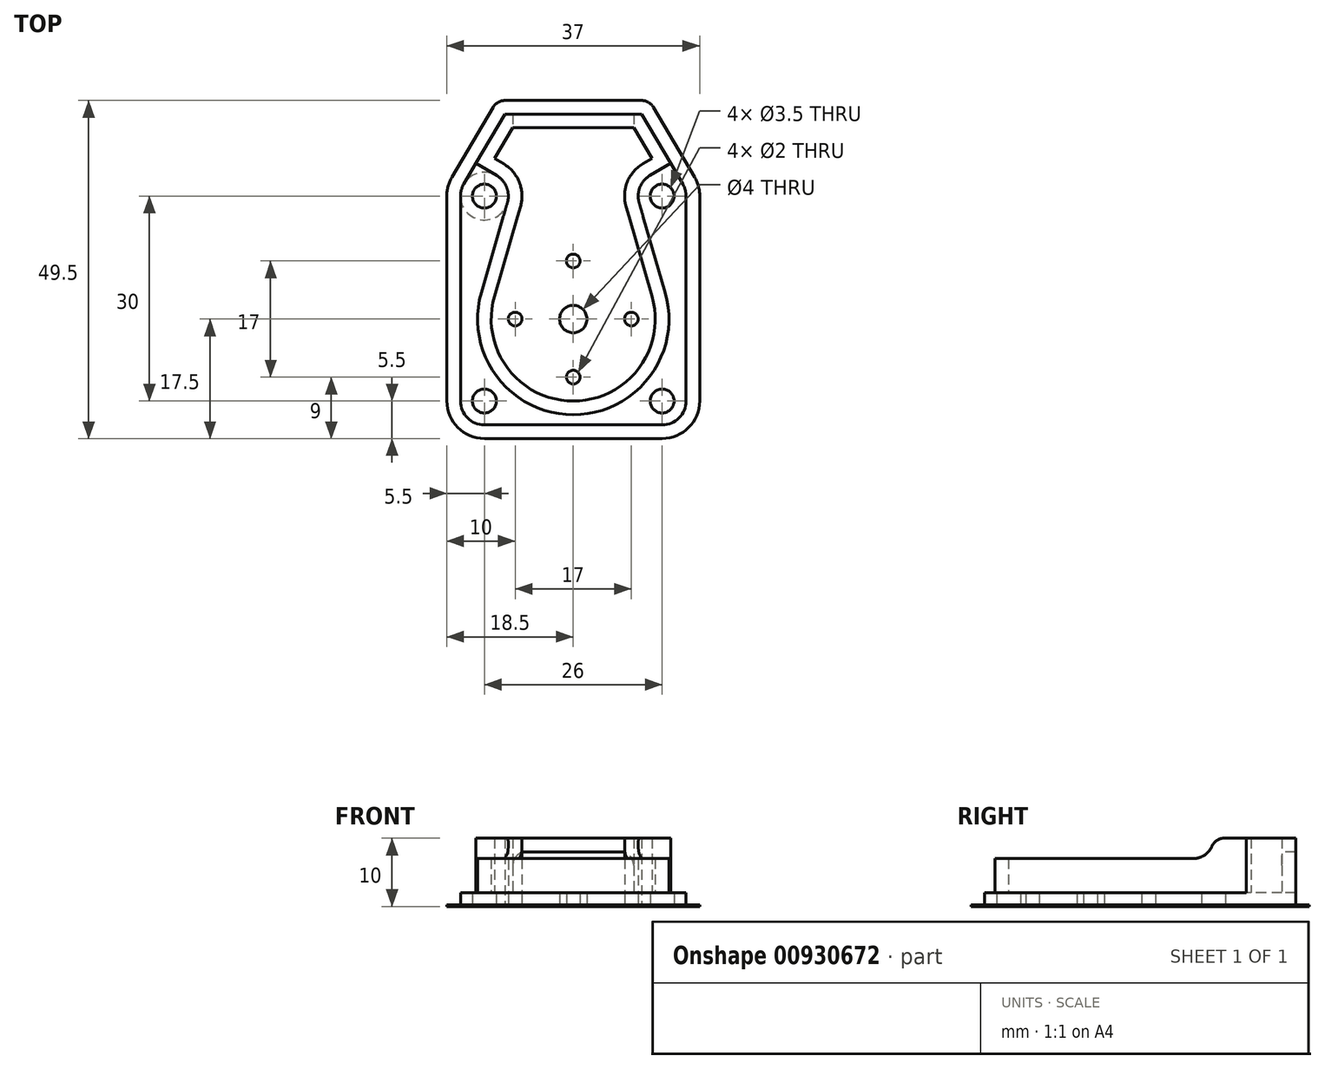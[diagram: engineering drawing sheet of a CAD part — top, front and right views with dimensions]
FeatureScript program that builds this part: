
annotation { "Feature Type Name" : "Feature", "Feature Type Description" : "" }
export const myFeature = defineFeature(function(context is Context, id is Id, definition is map)
    precondition{}
    {
        {
            var Q0;
            Q0=qCreatedBy(makeId("Top.planeOp"),FACE);
            var sketch = newSketch(context, id + "F0", { "sketchPlane" : qUnion([Q0])});
            skCircle(sketch, "E0", {"center": v(0, 0) * mm, "radius": 1.75 * mm});
            skCircle(sketch, "E1", {"center": v(0, 30) * mm, "radius": 1.75 * mm});
            skCircle(sketch, "E2", {"center": v(26, 30) * mm, "radius": 1.75 * mm});
            skCircle(sketch, "E3", {"center": v(26, 0) * mm, "radius": 1.75 * mm});
            skLineSegment(sketch, "E4.left", {"start": v(0, 30) * mm, "end": v(0, 0) * mm, "construction": true});
            skCircle(sketch, "E5", {"center": v(13, 12) * mm, "radius": 9.85 * mm, "construction": true});
            skLineSegment(sketch, "E6", {"start": v(13, 21.85) * mm, "end": v(13, 2.15) * mm, "construction": true});
            skLineSegment(sketch, "E7", {"start": v(3.15, 12) * mm, "end": v(22.85, 12) * mm, "construction": true});
            skCircle(sketch, "E8", {"center": v(13, 12) * mm, "radius": 2 * mm});
            skCircle(sketch, "E9", {"center": v(4.5, 12) * mm, "radius": 1 * mm});
            skCircle(sketch, "E10", {"center": v(21.5, 12) * mm, "radius": 1 * mm});
            skCircle(sketch, "E11", {"center": v(13, 20.5) * mm, "radius": 1 * mm});
            skCircle(sketch, "E12", {"center": v(13, 3.5) * mm, "radius": 1 * mm});
            skLineSegment(sketch, "E13", {"start": v(3, 42) * mm, "end": v(23, 42) * mm});
            skLineSegment(sketch, "E14", {"start": v(0, 30) * mm, "end": v(26, 30) * mm, "construction": true});
            skLineSegment(sketch, "E15", {"start": v(0, 0) * mm, "end": v(26, 0) * mm, "construction": true});
            skLineSegment(sketch, "E16.trimOffspring", {"start": v(-3.02, 31.77) * mm, "end": v(3, 42) * mm});
            skLineSegment(sketch, "E17.trimOffspring", {"start": v(29.02, 31.77) * mm, "end": v(23, 42) * mm});
            skLineSegment(sketch, "E18", {"start": v(26, 30) * mm, "end": v(26, 0) * mm, "construction": true});
            skLineSegment(sketch, "E19", {"start": v(-3.5, 30) * mm, "end": v(-3.5, 0) * mm});
            skLineSegment(sketch, "E20", {"start": v(0, -3.5) * mm, "end": v(26, -3.5) * mm});
            skLineSegment(sketch, "E21", {"start": v(29.5, 30) * mm, "end": v(29.5, 0) * mm});
            skArc(sketch, "E22", {"start": v(-3.5, 0) * mm, "mid": v(-2.47, -2.47) * mm, "end": v(0, -3.5) * mm});
            skArc(sketch, "E23", {"start": v(26, -3.5) * mm, "mid": v(28.47, -2.47) * mm, "end": v(29.5, 0) * mm});
            skArc(sketch, "E24", {"start": v(-3.02, 31.77) * mm, "mid": v(-3.38, 30.92) * mm, "end": v(-3.5, 30) * mm});
            skArc(sketch, "E25", {"start": v(29.5, 30) * mm, "mid": v(29.38, 30.92) * mm, "end": v(29.02, 31.77) * mm});
            skSolve(sketch);
        }
        {
            var Q0;
            Q0=qSketchRegion(id+"F0",true);
            extrude(context, id + "F1", {"entities" : qUnion([Q0]), "depth" : 2 * mm, "offsetDistance" : 25 * mm});
        }
        {
            var Q0;
            Q0=makeQuery(id+"F1.opExtrude","CAP_FACE",FACE,{"disambiguationData":[OSD([sQuery(id+"F0.wireOp",EDGE,"E0"),sQuery(id+"F0.wireOp",EDGE,"E1"),sQuery(id+"F0.wireOp",EDGE,"E2"),sQuery(id+"F0.wireOp",EDGE,"E3"),sQuery(id+"F0.wireOp",EDGE,"E8"),sQuery(id+"F0.wireOp",EDGE,"E9"),sQuery(id+"F0.wireOp",EDGE,"E10"),sQuery(id+"F0.wireOp",EDGE,"E11"),sQuery(id+"F0.wireOp",EDGE,"E12"),sQuery(id+"F0.wireOp",EDGE,"E13"),sQuery(id+"F0.wireOp",EDGE,"E16.trimOffspring"),sQuery(id+"F0.wireOp",EDGE,"E17.trimOffspring"),sQuery(id+"F0.wireOp",EDGE,"E19"),sQuery(id+"F0.wireOp",EDGE,"E20"),sQuery(id+"F0.wireOp",EDGE,"E21"),sQuery(id+"F0.wireOp",EDGE,"E22"),sQuery(id+"F0.wireOp",EDGE,"E23"),sQuery(id+"F0.wireOp",EDGE,"E24"),sQuery(id+"F0.wireOp",EDGE,"E25")])],"isStart":false});
            var sketch = newSketch(context, id + "F2", { "sketchPlane" : qUnion([Q0])});
            skLineSegment(sketch, "E26", {"start": v(0, 30) * mm, "end": v(26, 30) * mm, "construction": true});
            skLineSegment(sketch, "E27", {"start": v(3, 42) * mm, "end": v(23, 42) * mm});
            skLineSegment(sketch, "E28", {"start": v(23, 42) * mm, "end": v(27.24, 34.8) * mm});
            skLineSegment(sketch, "E29", {"start": v(27.24, 34.8) * mm, "end": v(24.23, 33.02) * mm});
            skArc(sketch, "E30", {"start": v(24.23, 33.02) * mm, "mid": v(22.75, 31.3) * mm, "end": v(22.64, 29.02) * mm});
            skArc(sketch, "E31", {"start": v(3.36, 29.02) * mm, "mid": v(3.25, 31.3) * mm, "end": v(1.77, 33.02) * mm});
            skLineSegment(sketch, "E32", {"start": v(3, 42) * mm, "end": v(-1.24, 34.8) * mm});
            skLineSegment(sketch, "E33", {"start": v(-1.24, 34.8) * mm, "end": v(1.77, 33.02) * mm});
            skLineSegment(sketch, "E34", {"start": v(4.14, 40) * mm, "end": v(1.5, 35.5) * mm});
            skLineSegment(sketch, "E35", {"start": v(1.5, 35.5) * mm, "end": v(2.79, 34.74) * mm});
            skLineSegment(sketch, "E36", {"start": v(4.14, 40) * mm, "end": v(21.86, 40) * mm});
            skLineSegment(sketch, "E37", {"start": v(21.86, 40) * mm, "end": v(24.5, 35.5) * mm});
            skLineSegment(sketch, "E38", {"start": v(24.5, 35.5) * mm, "end": v(23.21, 34.74) * mm});
            skArc(sketch, "E39", {"start": v(5.28, 28.47) * mm, "mid": v(5.11, 32.03) * mm, "end": v(2.79, 34.74) * mm});
            skArc(sketch, "E40", {"start": v(23.21, 34.74) * mm, "mid": v(20.89, 32.03) * mm, "end": v(20.72, 28.47) * mm});
            skArc(sketch, "E41", {"start": v(1.48, 15.34) * mm, "mid": v(13, 0) * mm, "end": v(24.52, 15.34) * mm});
            skArc(sketch, "E42", {"start": v(-0.45, 15.9) * mm, "mid": v(13, -2) * mm, "end": v(26.45, 15.9) * mm});
            skLineSegment(sketch, "E43", {"start": v(-0.45, 15.9) * mm, "end": v(3.36, 29.02) * mm});
            skLineSegment(sketch, "E44", {"start": v(22.64, 29.02) * mm, "end": v(26.45, 15.9) * mm});
            skLineSegment(sketch, "E45", {"start": v(20.72, 28.47) * mm, "end": v(24.52, 15.34) * mm});
            skLineSegment(sketch, "E46", {"start": v(5.28, 28.47) * mm, "end": v(1.48, 15.34) * mm});
            skSolve(sketch);
        }
        {
            var Q0;
            Q0=qSketchRegion(id+"F2",true);
            extrude(context, id + "F3", {"entities" : qUnion([Q0]), "operationType" : NewBodyOperationType.ADD, "depth" : 8 * mm, "offsetDistance" : 25 * mm});
        }
        {
            var Q0;
            Q0=makeQuery(id+"F3.opExtrude","SWEPT_FACE",FACE,{"disambiguationData":[OSD([sQuery(id+"F2.wireOp",EDGE,"E36")])]});
            var sketch = newSketch(context, id + "F4", { "sketchPlane" : qUnion([Q0])});
            skLineSegment(sketch, "E47.bottom", {"start": v(4.14, 2) * mm, "end": v(21.86, 2) * mm});
            skLineSegment(sketch, "E47.top", {"start": v(4.14, 8) * mm, "end": v(21.86, 8) * mm});
            skLineSegment(sketch, "E47.left", {"start": v(4.14, 2) * mm, "end": v(4.14, 8) * mm});
            skLineSegment(sketch, "E47.right", {"start": v(21.86, 2) * mm, "end": v(21.86, 8) * mm});
            skSolve(sketch);
        }
        {
            var Q0;
            Q0=qSketchRegion(id+"F4",true);
            extrude(context, id + "F5", {"entities" : qUnion([Q0]), "operationType" : NewBodyOperationType.REMOVE, "endBound" : BoundingType.UP_TO_NEXT, "oppositeDirection" : true, "depth" : 25 * mm, "offsetDistance" : 25 * mm});
        }
        {
            var Q0;
            Q0=makeQuery(id+"F5.boolean.opBoolean","COPY",EDGE,{"derivedFrom":makeQuery(id+"F5.opExtrude","SWEPT_EDGE",EDGE,{"disambiguationData":[OSD([sQuery(id+"F2.wireOp",EDGE,"E34"),sQuery(id+"F2.wireOp",EDGE,"E36"),sQuery(id+"F4.wireOp",EDGE,"E47.top"),sQuery(id+"F4.wireOp",EDGE,"E47.left")])]})});
            var Q1;
            Q1=makeQuery(id+"FvPu7uBZYHSXlxQ_1.boolean.opBoolean","COPY",EDGE,{"derivedFrom":makeQuery(id+"FvPu7uBZYHSXlxQ_1.opExtrude","SWEPT_EDGE",EDGE,{"disambiguationData":[OSD([sQuery(id+"F2.wireOp",EDGE,"87owH7vI-DY4W-UaA8-oZaw-rFrzevB4dvaM"),sQuery(id+"F2.wireOp",EDGE,"E39"),sQuery(id+"FQrBlxE3tJIOwN5_1.wireOp",EDGE,"wGyyUJUZ-AgT6-l7fz-nEv1-yPwmvjUjWFtQ.top"),sQuery(id+"FQrBlxE3tJIOwN5_1.wireOp",EDGE,"wGyyUJUZ-AgT6-l7fz-nEv1-yPwmvjUjWFtQ.right")])]})});
            var Q2;
            Q2=makeQuery(id+"FvPu7uBZYHSXlxQ_1.boolean.opBoolean","COPY",EDGE,{"derivedFrom":makeQuery(id+"FvPu7uBZYHSXlxQ_1.opExtrude","SWEPT_EDGE",EDGE,{"disambiguationData":[OSD([sQuery(id+"F2.wireOp",EDGE,"87owH7vI-DY4W-UaA8-oZaw-rFrzevB4dvaM"),sQuery(id+"F2.wireOp",EDGE,"E40"),sQuery(id+"FQrBlxE3tJIOwN5_1.wireOp",EDGE,"wGyyUJUZ-AgT6-l7fz-nEv1-yPwmvjUjWFtQ.top"),sQuery(id+"FQrBlxE3tJIOwN5_1.wireOp",EDGE,"wGyyUJUZ-AgT6-l7fz-nEv1-yPwmvjUjWFtQ.left")])]})});
            var Q3;
            Q3=makeQuery(id+"F5.boolean.opBoolean","COPY",EDGE,{"derivedFrom":makeQuery(id+"F5.opExtrude","SWEPT_EDGE",EDGE,{"disambiguationData":[OSD([sQuery(id+"F2.wireOp",EDGE,"E36"),sQuery(id+"F2.wireOp",EDGE,"E37"),sQuery(id+"F4.wireOp",EDGE,"E47.top"),sQuery(id+"F4.wireOp",EDGE,"E47.right")])]})});
            fillet(context, id + "F6", {"entities" : qUnion([Q0, Q1, Q2, Q3]), "radius" : 2 * mm, "tangentPropagation" : true, "allowEdgeOverflow" : false});
        }
        {
            var Q0;
            Q0=makeQuery(id+"F3.opExtrude","CAP_FACE",FACE,{"disambiguationData":[OSD([sQuery(id+"F2.wireOp",EDGE,"87owH7vI-DY4W-UaA8-oZaw-rFrzevB4dvaM"),sQuery(id+"F2.wireOp",EDGE,"E27"),sQuery(id+"F2.wireOp",EDGE,"E28"),sQuery(id+"F2.wireOp",EDGE,"E29"),sQuery(id+"F2.wireOp",EDGE,"E30"),sQuery(id+"F2.wireOp",EDGE,"E31"),sQuery(id+"F2.wireOp",EDGE,"E32"),sQuery(id+"F2.wireOp",EDGE,"E33"),sQuery(id+"F2.wireOp",EDGE,"E34"),sQuery(id+"F2.wireOp",EDGE,"E35"),sQuery(id+"F2.wireOp",EDGE,"E36"),sQuery(id+"F2.wireOp",EDGE,"E37"),sQuery(id+"F2.wireOp",EDGE,"E38"),sQuery(id+"F2.wireOp",EDGE,"E39"),sQuery(id+"F2.wireOp",EDGE,"E40"),sQuery(id+"F2.wireOp",EDGE,"E41"),sQuery(id+"F2.wireOp",EDGE,"E42"),sQuery(id+"F2.wireOp",EDGE,"E43"),sQuery(id+"F2.wireOp",EDGE,"E44"),sQuery(id+"F2.wireOp",EDGE,"n5o2zeqW-Y6Ct-pq06-zOnF-6KBVIWVYcsxy"),sQuery(id+"F2.wireOp",EDGE,"E45"),sQuery(id+"F2.wireOp",EDGE,"E46")])],"isStart":false});
            var sketch = newSketch(context, id + "F7", { "sketchPlane" : qUnion([Q0])});
            skLineSegment(sketch, "E48", {"start": v(5.28, 28.47) * mm, "end": v(1.48, 15.34) * mm});
            skLineSegment(sketch, "E49", {"start": v(3.36, 29.02) * mm, "end": v(-0.45, 15.9) * mm});
            skLineSegment(sketch, "E50", {"start": v(20.72, 28.47) * mm, "end": v(24.52, 15.34) * mm});
            skLineSegment(sketch, "E51", {"start": v(22.64, 29.02) * mm, "end": v(26.45, 15.9) * mm});
            skArc(sketch, "E52", {"start": v(1.48, 15.34) * mm, "mid": v(13, 0) * mm, "end": v(24.52, 15.34) * mm});
            skArc(sketch, "E53", {"start": v(-0.45, 15.9) * mm, "mid": v(13, -2) * mm, "end": v(26.45, 15.9) * mm});
            skLineSegment(sketch, "E54", {"start": v(3.5, 30) * mm, "end": v(5.5, 30) * mm});
            skLineSegment(sketch, "E55", {"start": v(20.5, 30) * mm, "end": v(22.5, 30) * mm});
            skArc(sketch, "E56", {"start": v(5.28, 28.47) * mm, "mid": v(5.45, 29.23) * mm, "end": v(5.5, 30) * mm});
            skArc(sketch, "E57", {"start": v(3.36, 29.02) * mm, "mid": v(3.47, 29.5) * mm, "end": v(3.5, 30) * mm});
            skArc(sketch, "E58", {"start": v(20.5, 30) * mm, "mid": v(20.55, 29.23) * mm, "end": v(20.72, 28.47) * mm});
            skArc(sketch, "E59", {"start": v(22.5, 30) * mm, "mid": v(22.53, 29.5) * mm, "end": v(22.64, 29.02) * mm});
            skSolve(sketch);
        }
        {
            var Q0;
            Q0=qSketchRegion(id+"F7",true);
            extrude(context, id + "F8", {"entities" : qUnion([Q0]), "operationType" : NewBodyOperationType.REMOVE, "oppositeDirection" : true, "depth" : 3 * mm, "offsetDistance" : 25 * mm});
        }
        {
            var Q0;
            Q0=makeQuery(id+"F8.boolean.opBoolean","COPY",EDGE,{"derivedFrom":makeQuery(id+"F8.opExtrude","CAP_EDGE",EDGE,{"disambiguationData":[OSD([sQuery(id+"F7.wireOp",EDGE,"E54")])],"isStart":false})});
            var Q1;
            Q1=makeQuery(id+"F8.boolean.opBoolean","COPY",EDGE,{"derivedFrom":makeQuery(id+"F8.opExtrude","CAP_EDGE",EDGE,{"disambiguationData":[OSD([sQuery(id+"F7.wireOp",EDGE,"E55")])],"isStart":false})});
            fillet(context, id + "F9", {"entities" : qUnion([Q0, Q1]), "radius" : 3 * mm, "tangentPropagation" : true, "allowEdgeOverflow" : false});
        }
        {
            var Q0;
            Q0=makeQuery(id+"F9.opFillet","BLEND_EDGE",EDGE,{"blendedFrom":[makeQuery(id+"F8.boolean.opBoolean","COPY",EDGE,{"derivedFrom":makeQuery(id+"F8.opExtrude","CAP_EDGE",EDGE,{"disambiguationData":[OSD([sQuery(id+"F7.wireOp",EDGE,"E54")])],"isStart":false})}),makeQuery(id+"F3.opExtrude","CAP_FACE",FACE,{"disambiguationData":[OSD([sQuery(id+"F2.wireOp",EDGE,"E27"),sQuery(id+"F2.wireOp",EDGE,"E28"),sQuery(id+"F2.wireOp",EDGE,"E29"),sQuery(id+"F2.wireOp",EDGE,"E30"),sQuery(id+"F2.wireOp",EDGE,"E31"),sQuery(id+"F2.wireOp",EDGE,"E32"),sQuery(id+"F2.wireOp",EDGE,"E33"),sQuery(id+"F2.wireOp",EDGE,"E34"),sQuery(id+"F2.wireOp",EDGE,"E35"),sQuery(id+"F2.wireOp",EDGE,"E36"),sQuery(id+"F2.wireOp",EDGE,"E37"),sQuery(id+"F2.wireOp",EDGE,"E38"),sQuery(id+"F2.wireOp",EDGE,"E39"),sQuery(id+"F2.wireOp",EDGE,"E40"),sQuery(id+"F2.wireOp",EDGE,"E41"),sQuery(id+"F2.wireOp",EDGE,"E42"),sQuery(id+"F2.wireOp",EDGE,"E43"),sQuery(id+"F2.wireOp",EDGE,"E44"),sQuery(id+"F2.wireOp",EDGE,"E45"),sQuery(id+"F2.wireOp",EDGE,"E46")])],"isStart":false})],"blendedInto":[makeQuery(id+"F3.opExtrude","CAP_FACE",FACE,{"disambiguationData":[OSD([sQuery(id+"F2.wireOp",EDGE,"E27"),sQuery(id+"F2.wireOp",EDGE,"E28"),sQuery(id+"F2.wireOp",EDGE,"E29"),sQuery(id+"F2.wireOp",EDGE,"E30"),sQuery(id+"F2.wireOp",EDGE,"E31"),sQuery(id+"F2.wireOp",EDGE,"E32"),sQuery(id+"F2.wireOp",EDGE,"E33"),sQuery(id+"F2.wireOp",EDGE,"E34"),sQuery(id+"F2.wireOp",EDGE,"E35"),sQuery(id+"F2.wireOp",EDGE,"E36"),sQuery(id+"F2.wireOp",EDGE,"E37"),sQuery(id+"F2.wireOp",EDGE,"E38"),sQuery(id+"F2.wireOp",EDGE,"E39"),sQuery(id+"F2.wireOp",EDGE,"E40"),sQuery(id+"F2.wireOp",EDGE,"E41"),sQuery(id+"F2.wireOp",EDGE,"E42"),sQuery(id+"F2.wireOp",EDGE,"E43"),sQuery(id+"F2.wireOp",EDGE,"E44"),sQuery(id+"F2.wireOp",EDGE,"E45"),sQuery(id+"F2.wireOp",EDGE,"E46")])],"isStart":false})]});
            var Q1;
            Q1=makeQuery(id+"F9.opFillet","BLEND_EDGE",EDGE,{"blendedFrom":[makeQuery(id+"F8.boolean.opBoolean","COPY",EDGE,{"derivedFrom":makeQuery(id+"F8.opExtrude","CAP_EDGE",EDGE,{"disambiguationData":[OSD([sQuery(id+"F7.wireOp",EDGE,"E55")])],"isStart":false})}),makeQuery(id+"F3.opExtrude","CAP_FACE",FACE,{"disambiguationData":[OSD([sQuery(id+"F2.wireOp",EDGE,"E27"),sQuery(id+"F2.wireOp",EDGE,"E28"),sQuery(id+"F2.wireOp",EDGE,"E29"),sQuery(id+"F2.wireOp",EDGE,"E30"),sQuery(id+"F2.wireOp",EDGE,"E31"),sQuery(id+"F2.wireOp",EDGE,"E32"),sQuery(id+"F2.wireOp",EDGE,"E33"),sQuery(id+"F2.wireOp",EDGE,"E34"),sQuery(id+"F2.wireOp",EDGE,"E35"),sQuery(id+"F2.wireOp",EDGE,"E36"),sQuery(id+"F2.wireOp",EDGE,"E37"),sQuery(id+"F2.wireOp",EDGE,"E38"),sQuery(id+"F2.wireOp",EDGE,"E39"),sQuery(id+"F2.wireOp",EDGE,"E40"),sQuery(id+"F2.wireOp",EDGE,"E41"),sQuery(id+"F2.wireOp",EDGE,"E42"),sQuery(id+"F2.wireOp",EDGE,"E43"),sQuery(id+"F2.wireOp",EDGE,"E44"),sQuery(id+"F2.wireOp",EDGE,"E45"),sQuery(id+"F2.wireOp",EDGE,"E46")])],"isStart":false})],"blendedInto":[makeQuery(id+"F3.opExtrude","CAP_FACE",FACE,{"disambiguationData":[OSD([sQuery(id+"F2.wireOp",EDGE,"E27"),sQuery(id+"F2.wireOp",EDGE,"E28"),sQuery(id+"F2.wireOp",EDGE,"E29"),sQuery(id+"F2.wireOp",EDGE,"E30"),sQuery(id+"F2.wireOp",EDGE,"E31"),sQuery(id+"F2.wireOp",EDGE,"E32"),sQuery(id+"F2.wireOp",EDGE,"E33"),sQuery(id+"F2.wireOp",EDGE,"E34"),sQuery(id+"F2.wireOp",EDGE,"E35"),sQuery(id+"F2.wireOp",EDGE,"E36"),sQuery(id+"F2.wireOp",EDGE,"E37"),sQuery(id+"F2.wireOp",EDGE,"E38"),sQuery(id+"F2.wireOp",EDGE,"E39"),sQuery(id+"F2.wireOp",EDGE,"E40"),sQuery(id+"F2.wireOp",EDGE,"E41"),sQuery(id+"F2.wireOp",EDGE,"E42"),sQuery(id+"F2.wireOp",EDGE,"E43"),sQuery(id+"F2.wireOp",EDGE,"E44"),sQuery(id+"F2.wireOp",EDGE,"E45"),sQuery(id+"F2.wireOp",EDGE,"E46")])],"isStart":false})]});
            fillet(context, id + "F10", {"entities" : qUnion([Q0, Q1]), "radius" : 2 * mm, "tangentPropagation" : true, "allowEdgeOverflow" : false});
        }
        {
            var Q0;
            Q0=makeQuery(id+"F1.opExtrude","CAP_FACE",FACE,{"disambiguationData":[OSD([sQuery(id+"F0.wireOp",EDGE,"E0"),sQuery(id+"F0.wireOp",EDGE,"E1"),sQuery(id+"F0.wireOp",EDGE,"E2"),sQuery(id+"F0.wireOp",EDGE,"E3"),sQuery(id+"F0.wireOp",EDGE,"E8"),sQuery(id+"F0.wireOp",EDGE,"E9"),sQuery(id+"F0.wireOp",EDGE,"E10"),sQuery(id+"F0.wireOp",EDGE,"E11"),sQuery(id+"F0.wireOp",EDGE,"E12"),sQuery(id+"F0.wireOp",EDGE,"E13"),sQuery(id+"F0.wireOp",EDGE,"E16.trimOffspring"),sQuery(id+"F0.wireOp",EDGE,"E17.trimOffspring"),sQuery(id+"F0.wireOp",EDGE,"E19"),sQuery(id+"F0.wireOp",EDGE,"E20"),sQuery(id+"F0.wireOp",EDGE,"E21"),sQuery(id+"F0.wireOp",EDGE,"E22"),sQuery(id+"F0.wireOp",EDGE,"E23"),sQuery(id+"F0.wireOp",EDGE,"E24"),sQuery(id+"F0.wireOp",EDGE,"E25")])],"isStart":true});
            var sketch = newSketch(context, id + "F11", { "sketchPlane" : qUnion([Q0])});
            skLineSegment(sketch, "E60", {"start": v(-3.5, 0) * mm, "end": v(-3.5, -30) * mm});
            skLineSegment(sketch, "E61", {"start": v(-3.02, -31.77) * mm, "end": v(3, -42) * mm});
            skLineSegment(sketch, "E62", {"start": v(3, -42) * mm, "end": v(23, -42) * mm});
            skLineSegment(sketch, "E63", {"start": v(23, -42) * mm, "end": v(29.02, -31.77) * mm});
            skLineSegment(sketch, "E64", {"start": v(29.5, 0) * mm, "end": v(29.5, -30) * mm});
            skLineSegment(sketch, "E65", {"start": v(0, 3.5) * mm, "end": v(26, 3.5) * mm});
            skArc(sketch, "E66", {"start": v(0, 3.5) * mm, "mid": v(-2.47, 2.47) * mm, "end": v(-3.5, 0) * mm});
            skArc(sketch, "E67", {"start": v(29.5, 0) * mm, "mid": v(28.47, 2.47) * mm, "end": v(26, 3.5) * mm});
            skArc(sketch, "E68", {"start": v(29.02, -31.77) * mm, "mid": v(29.38, -30.92) * mm, "end": v(29.5, -30) * mm});
            skArc(sketch, "E69", {"start": v(-3.5, -30) * mm, "mid": v(-3.38, -30.92) * mm, "end": v(-3.02, -31.77) * mm});
            skLineSegment(sketch, "E70", {"start": v(-5.5, 0) * mm, "end": v(-5.5, -30) * mm});
            skLineSegment(sketch, "E71", {"start": v(0, 5.5) * mm, "end": v(26, 5.5) * mm});
            skLineSegment(sketch, "E72", {"start": v(31.5, 0) * mm, "end": v(31.5, -30) * mm});
            skLineSegment(sketch, "E73", {"start": v(-4.74, -32.79) * mm, "end": v(1.28, -43.01) * mm});
            skLineSegment(sketch, "E74", {"start": v(3, -44) * mm, "end": v(23, -44) * mm});
            skLineSegment(sketch, "E75", {"start": v(24.72, -43.01) * mm, "end": v(30.74, -32.79) * mm});
            skArc(sketch, "E76", {"start": v(-5.5, -30) * mm, "mid": v(-5.3, -31.45) * mm, "end": v(-4.74, -32.79) * mm});
            skArc(sketch, "E77", {"start": v(30.74, -32.79) * mm, "mid": v(31.3, -31.45) * mm, "end": v(31.5, -30) * mm});
            skArc(sketch, "E78", {"start": v(0, 5.5) * mm, "mid": v(-3.89, 3.89) * mm, "end": v(-5.5, 0) * mm});
            skArc(sketch, "E79", {"start": v(31.5, 0) * mm, "mid": v(29.89, 3.89) * mm, "end": v(26, 5.5) * mm});
            skArc(sketch, "E80", {"start": v(1.28, -43.01) * mm, "mid": v(2, -43.74) * mm, "end": v(3, -44) * mm});
            skArc(sketch, "E81", {"start": v(23, -44) * mm, "mid": v(24, -43.74) * mm, "end": v(24.72, -43.01) * mm});
            skSolve(sketch);
        }
        {
            var Q0;
            Q0=qSketchRegion(id+"F11",true);
            extrude(context, id + "F12", {"entities" : qUnion([Q0]), "operationType" : NewBodyOperationType.ADD, "oppositeDirection" : true, "depth" : 0.2 * mm, "offsetDistance" : 25 * mm});
        }
    });
